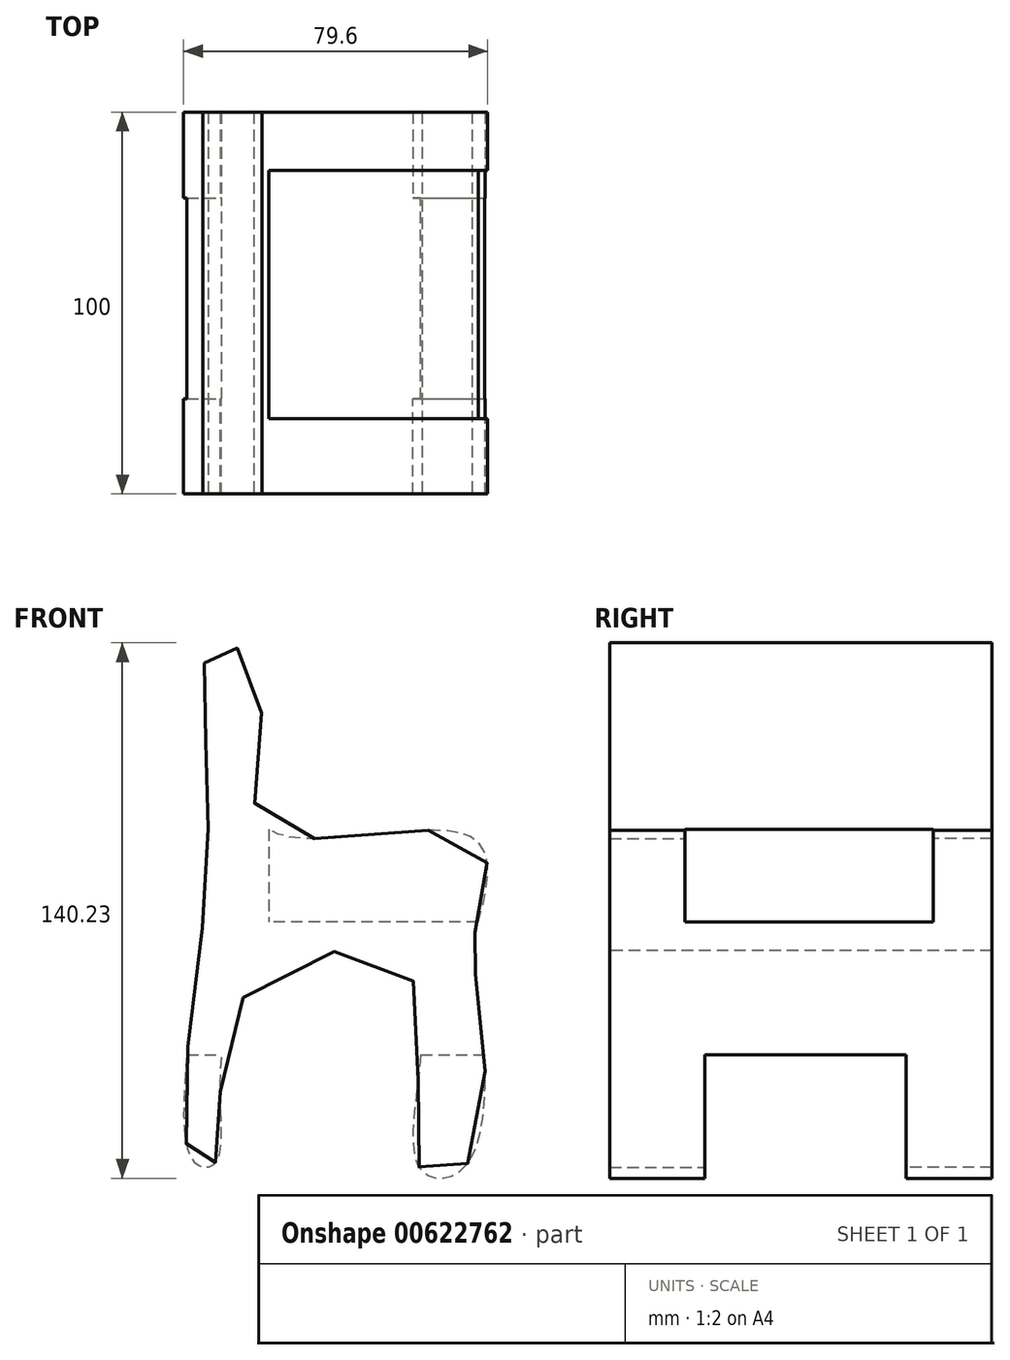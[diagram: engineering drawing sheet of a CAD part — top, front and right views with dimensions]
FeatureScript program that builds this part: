
annotation { "Feature Type Name" : "Feature", "Feature Type Description" : "" }
export const myFeature = defineFeature(function(context is Context, id is Id, definition is map)
    precondition{}
    {
        {
            var Q0;
            Q0=qCreatedBy(makeId("Front.planeOp"),FACE);
            var sketch = newSketch(context, id + "F0", { "sketchPlane" : qUnion([Q0])});
            skFitSpline(sketch, "E0", {"points": [v(-41.56, 45.4) * mm, v(-42.74, -6.36) * mm, v(-44.81, -64.34) * mm, v(-38.6, -64.34) * mm, v(-32.69, -22.92) * mm, v(11.68, -15.53) * mm, v(14.05, -65.52) * mm, v(27.36, -64.63) * mm, v(28.84, -13.46) * mm, v(28.84, -5.18) * mm, v(29.14, 19.67) * mm, v(-25.3, 22.63) * mm, v(-27.36, 61.38) * mm, v(-39.2, 70.84) * mm, v(-41.56, 45.4) * mm]});
            skSolve(sketch);
        }
        {
            var Q0;
            Q0=makeQuery(id+"F0.imprint","IMPRINT",FACE,{"disambiguationData":[TD([[makeQuery(id+"F0.imprint","IMPRINT",EDGE,{"derivedFrom":sQuery(id+"F0.wireOp",EDGE,"E0")}),1.0]])]});
            extrude(context, id + "F1", {"entities" : qUnion([Q0]), "depth" : 100 * mm, "offsetDistance" : 25 * mm});
        }
        {
            var Q0;
            Q0=qCreatedBy(makeId("Right.planeOp"),FACE);
            var sketch = newSketch(context, id + "F2", { "sketchPlane" : qUnion([Q0])});
            skLineSegment(sketch, "E1.bottom", {"start": v(-75.08, -36.68) * mm, "end": v(-22.42, -36.68) * mm});
            skLineSegment(sketch, "E1.top", {"start": v(-75.08, -69.2) * mm, "end": v(-22.42, -69.2) * mm});
            skLineSegment(sketch, "E1.left", {"start": v(-75.08, -36.68) * mm, "end": v(-75.08, -69.2) * mm});
            skLineSegment(sketch, "E1.right", {"start": v(-22.42, -36.68) * mm, "end": v(-22.42, -69.2) * mm});
            skSolve(sketch);
        }
        {
            var Q0;
            Q0 = qSketchRegion(id + "F2", true);
            extrude(context, id + "F3", {"entities" : qUnion([Q0]), "operationType" : NewBodyOperationType.REMOVE, "oppositeDirection" : true, "depth" : 100 * mm, "offsetDistance" : 25 * mm, "hasSecondDirection" : true, "secondDirectionOppositeDirection" : false, "secondDirectionDepth" : 65.9 * mm});
        }
        {
            var Q0;
            Q0=qCreatedBy(makeId("Right.planeOp"),FACE);
            var sketch = newSketch(context, id + "F4", { "sketchPlane" : qUnion([Q0])});
            skLineSegment(sketch, "E2.bottom", {"start": v(-80.28, 24.23) * mm, "end": v(-15.28, 24.23) * mm});
            skLineSegment(sketch, "E2.top", {"start": v(-80.28, -1.78) * mm, "end": v(-15.28, -1.78) * mm});
            skLineSegment(sketch, "E2.left", {"start": v(-80.28, 24.23) * mm, "end": v(-80.28, -1.78) * mm});
            skLineSegment(sketch, "E2.right", {"start": v(-15.28, 24.23) * mm, "end": v(-15.28, -1.78) * mm});
            skSolve(sketch);
        }
        {
            var Q0;
            Q0 = qSketchRegion(id + "F4", true);
            extrude(context, id + "F5", {"entities" : qUnion([Q0]), "operationType" : NewBodyOperationType.REMOVE, "depth" : 58.1 * mm, "offsetDistance" : 25 * mm, "hasSecondDirection" : true, "secondDirectionOppositeDirection" : true, "secondDirectionDepth" : 25 * mm});
        }
    });
